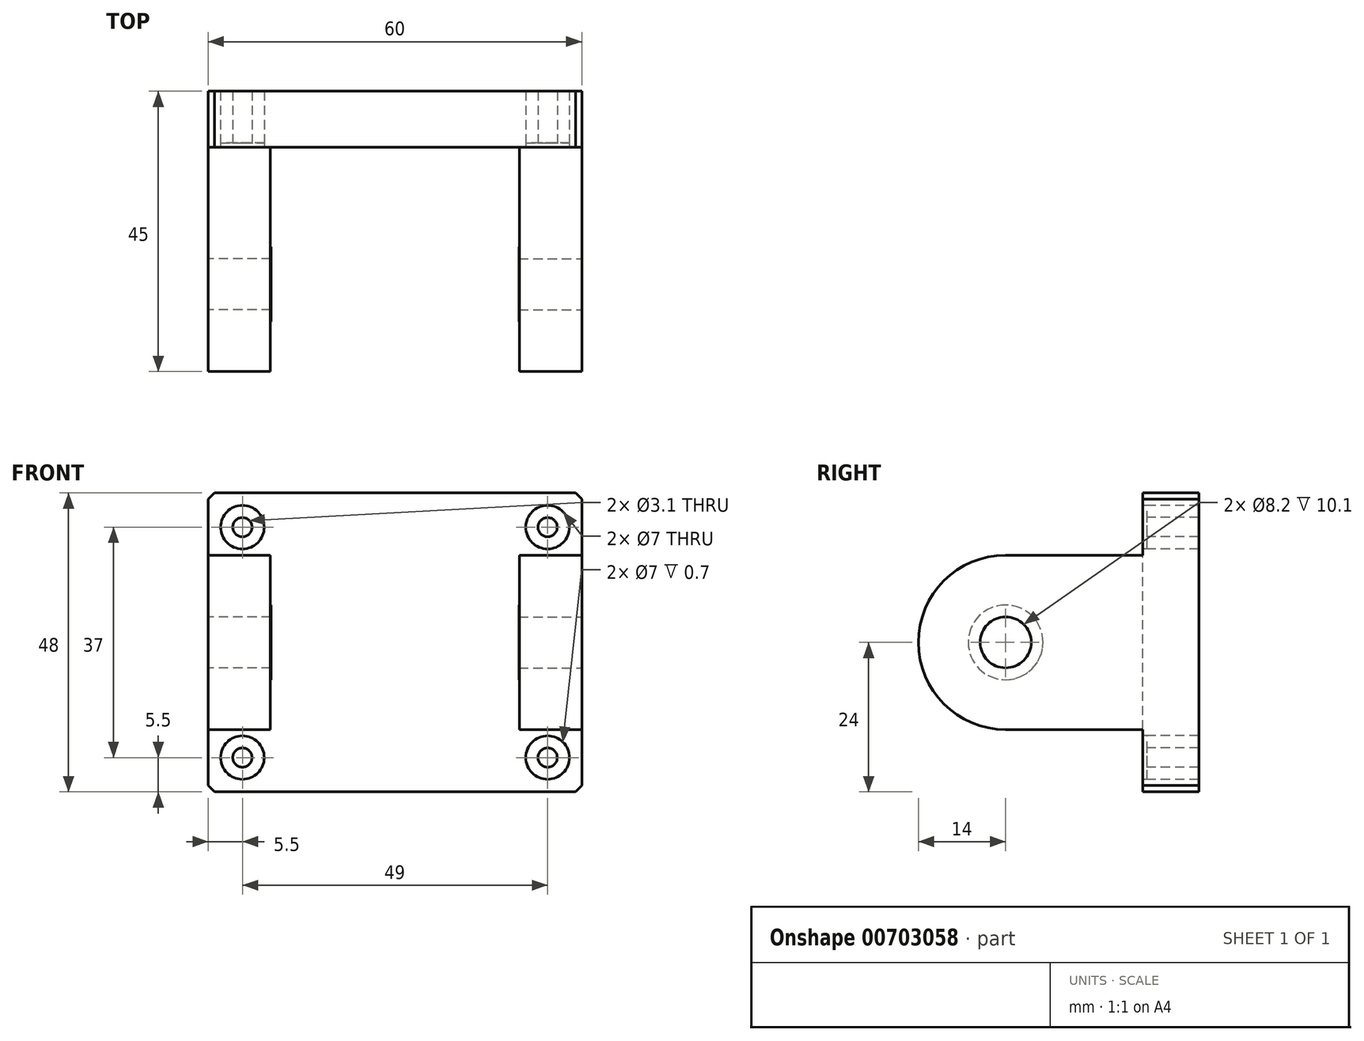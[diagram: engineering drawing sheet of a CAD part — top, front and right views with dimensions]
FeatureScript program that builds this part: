
annotation { "Feature Type Name" : "Feature", "Feature Type Description" : "" }
export const myFeature = defineFeature(function(context is Context, id is Id, definition is map)
    precondition{}
    {
        {
            var Q0;
            Q0=qCreatedBy(makeId("Front.planeOp"),FACE);
            var sketch = newSketch(context, id + "F0", { "sketchPlane" : qUnion([Q0])});
            skLineSegment(sketch, "E0.bottom", {"start": v(-20, 14) * mm, "end": v(20, 14) * mm});
            skLineSegment(sketch, "E0.top", {"start": v(-20, -14) * mm, "end": v(20, -14) * mm});
            skLineSegment(sketch, "E0.left", {"start": v(-20, 14) * mm, "end": v(-20, -14) * mm});
            skLineSegment(sketch, "E0.right", {"start": v(20, 14) * mm, "end": v(20, -14) * mm});
            skPoint(sketch, "E0.middle", {"position": v(0, 0) * mm});
            skLineSegment(sketch, "E1.0", {"start": v(-30, 24) * mm, "end": v(30, 24) * mm});
            skLineSegment(sketch, "E1.1", {"start": v(-30, 24) * mm, "end": v(-30, -24) * mm});
            skLineSegment(sketch, "E1.2", {"start": v(-30, -24) * mm, "end": v(30, -24) * mm});
            skLineSegment(sketch, "E1.3", {"start": v(30, 24) * mm, "end": v(30, -24) * mm});
            skSolve(sketch);
        }
        {
            var Q0;
            Q0=makeQuery(id+"F0.imprint","IMPRINT",FACE,{"disambiguationData":[TD([[makeQuery(id+"F0.imprint","IMPRINT",EDGE,{"derivedFrom":sQuery(id+"F0.wireOp",EDGE,"E0.bottom")}),1.0]])]});
            extrude(context, id + "F1", {"entities" : qUnion([Q0]), "depth" : 46 * mm, "offsetDistance" : 25 * mm});
        }
        {
            var Q0;
            Q0=makeQuery(id+"F1.opExtrude","SWEPT_FACE",FACE,{"disambiguationData":[OSD([sQuery(id+"F0.wireOp",EDGE,"E1.1")])]});
            var sketch = newSketch(context, id + "F2", { "sketchPlane" : qUnion([Q0])});
            skLineSegment(sketch, "E2", {"start": v(31, 24) * mm, "end": v(31, -24) * mm, "construction": true});
            skCircle(sketch, "E3", {"center": v(31, 0) * mm, "radius": 4.1 * mm});
            skSolve(sketch);
        }
        {
            var Q0;
            Q0=makeQuery(id+"F2.imprint","IMPRINT",FACE,{"disambiguationData":[TD([[makeQuery(id+"F2.imprint","IMPRINT",EDGE,{"derivedFrom":sQuery(id+"F2.wireOp",EDGE,"E3")}),1.0]])]});
            extrude(context, id + "F3", {"entities" : qUnion([Q0]), "operationType" : NewBodyOperationType.REMOVE, "oppositeDirection" : true, "depth" : 10 * mm, "offsetDistance" : 25 * mm});
        }
        {
            var Q0;
            Q0=makeQuery(id+"F1.opExtrude","SWEPT_FACE",FACE,{"disambiguationData":[OSD([sQuery(id+"F0.wireOp",EDGE,"E1.3")])]});
            var sketch = newSketch(context, id + "F4", { "sketchPlane" : qUnion([Q0])});
            skLineSegment(sketch, "E4", {"start": v(-31, -24) * mm, "end": v(-31, 24) * mm, "construction": true});
            skCircle(sketch, "E5", {"center": v(-31, 0) * mm, "radius": 4.1 * mm});
            skSolve(sketch);
        }
        {
            var Q0;
            Q0=makeQuery(id+"F4.imprint","IMPRINT",FACE,{"disambiguationData":[TD([[makeQuery(id+"F4.imprint","IMPRINT",EDGE,{"derivedFrom":sQuery(id+"F4.wireOp",EDGE,"E5")}),1.0]])]});
            extrude(context, id + "F5", {"entities" : qUnion([Q0]), "operationType" : NewBodyOperationType.REMOVE, "oppositeDirection" : true, "depth" : 10 * mm, "offsetDistance" : 25 * mm});
        }
        {
            var Q0;
            Q0=makeQuery(id+"F1.opExtrude","SWEPT_FACE",FACE,{"disambiguationData":[OSD([sQuery(id+"F0.wireOp",EDGE,"E0.left")])]});
            var sketch = newSketch(context, id + "F6", { "sketchPlane" : qUnion([Q0])});
            skCircle(sketch, "E6", {"center": v(-31, 0) * mm, "radius": 6 * mm});
            skSolve(sketch);
        }
        {
            var Q0;
            Q0=makeQuery(id+"F6.imprint","IMPRINT",FACE,{"disambiguationData":[TD([[makeQuery(id+"F6.imprint","IMPRINT",EDGE,{"derivedFrom":sQuery(id+"F6.wireOp",EDGE,"E6")}),1.0]])]});
            extrude(context, id + "F7", {"entities" : qUnion([Q0]), "operationType" : NewBodyOperationType.ADD, "depth" : 0.1 * mm, "offsetDistance" : 25 * mm});
        }
        {
            var Q0;
            Q0=makeQuery(id+"F1.opExtrude","SWEPT_FACE",FACE,{"disambiguationData":[OSD([sQuery(id+"F0.wireOp",EDGE,"E0.right")])]});
            var sketch = newSketch(context, id + "F8", { "sketchPlane" : qUnion([Q0])});
            skCircle(sketch, "E7", {"center": v(31, 0) * mm, "radius": 6 * mm});
            skSolve(sketch);
        }
        {
            var Q0;
            Q0=makeQuery(id+"F8.imprint","IMPRINT",FACE,{"disambiguationData":[TD([[makeQuery(id+"F8.imprint","IMPRINT",EDGE,{"derivedFrom":sQuery(id+"F8.wireOp",EDGE,"E7")}),1.0]])]});
            extrude(context, id + "F9", {"entities" : qUnion([Q0]), "operationType" : NewBodyOperationType.ADD, "depth" : 0.1 * mm, "offsetDistance" : 25 * mm});
        }
        {
            var Q0;
            Q0=makeQuery(id+"F1.opExtrude","CAP_FACE",FACE,{"disambiguationData":[OSD([sQuery(id+"F0.wireOp",EDGE,"E0.bottom"),sQuery(id+"F0.wireOp",EDGE,"E0.top"),sQuery(id+"F0.wireOp",EDGE,"E0.left"),sQuery(id+"F0.wireOp",EDGE,"E0.right"),sQuery(id+"F0.wireOp",EDGE,"E1.0"),sQuery(id+"F0.wireOp",EDGE,"E1.1"),sQuery(id+"F0.wireOp",EDGE,"E1.2"),sQuery(id+"F0.wireOp",EDGE,"E1.3")])],"isStart":false});
            var sketch = newSketch(context, id + "F10", { "sketchPlane" : qUnion([Q0])});
            skLineSegment(sketch, "E8", {"start": v(-20, 14) * mm, "end": v(-20, 24) * mm});
            skLineSegment(sketch, "E9", {"start": v(20, 14) * mm, "end": v(20, 24) * mm});
            skLineSegment(sketch, "E10", {"start": v(-20, -14) * mm, "end": v(-20, -24) * mm});
            skLineSegment(sketch, "E11", {"start": v(20, -14) * mm, "end": v(20, -24) * mm});
            skSolve(sketch);
        }
        {
            var Q0;
            {var subQ0=sQuery(id+"F10.wireOp",EDGE,"E8");Q0=makeQuery(id+"F10.imprint","IMPRINT",FACE,{"disambiguationData":[TD([[makeQuery(id+"F10.imprint","IMPRINT",EDGE,{"derivedFrom":subQ0}),-1.0]])]});}
            var Q1;
            {var subQ0=sQuery(id+"F10.wireOp",EDGE,"E10");Q1=makeQuery(id+"F10.imprint","IMPRINT",FACE,{"disambiguationData":[TD([[makeQuery(id+"F10.imprint","IMPRINT",EDGE,{"derivedFrom":subQ0}),1.0]])]});}
            extrude(context, id + "F11", {"entities" : qUnion([Q0, Q1]), "operationType" : NewBodyOperationType.REMOVE, "oppositeDirection" : true, "depth" : 15 * mm, "offsetDistance" : 25 * mm});
        }
        {
            var Q0;
            Q0=makeQuery(id+"F11.boolean.opBoolean","MERGE",FACE,{"derivedFrom":[makeQuery(id+"F1.opExtrude","SWEPT_FACE",FACE,{"disambiguationData":[OSD([sQuery(id+"F0.wireOp",EDGE,"E0.right")])]}),makeQuery(id+"F11.opExtrude","SWEPT_FACE",FACE,{"disambiguationData":[OSD([sQuery(id+"F10.wireOp",EDGE,"E9")])]}),makeQuery(id+"F11.opExtrude","SWEPT_FACE",FACE,{"disambiguationData":[OSD([sQuery(id+"F10.wireOp",EDGE,"E11")])]})]});
            var sketch = newSketch(context, id + "F12", { "sketchPlane" : qUnion([Q0])});
            skArc(sketch, "E12", {"start": v(31, -14) * mm, "mid": v(45, 0) * mm, "end": v(31, 14) * mm});
            skSolve(sketch);
        }
        {
            var Q0;
            Q0=makeQuery(id+"F11.boolean.opBoolean","MERGE",FACE,{"derivedFrom":[makeQuery(id+"F1.opExtrude","SWEPT_FACE",FACE,{"disambiguationData":[OSD([sQuery(id+"F0.wireOp",EDGE,"E0.left")])]}),makeQuery(id+"F11.opExtrude","SWEPT_FACE",FACE,{"disambiguationData":[OSD([sQuery(id+"F10.wireOp",EDGE,"E8")])]}),makeQuery(id+"F11.opExtrude","SWEPT_FACE",FACE,{"disambiguationData":[OSD([sQuery(id+"F10.wireOp",EDGE,"E10")])]})]});
            var sketch = newSketch(context, id + "F13", { "sketchPlane" : qUnion([Q0])});
            skArc(sketch, "E13", {"start": v(-31, 14) * mm, "mid": v(-45, 0) * mm, "end": v(-31, -14) * mm});
            skSolve(sketch);
        }
        {
            var Q0;
            Q0=makeQuery(id+"F13.imprint","IMPRINT",FACE,{"disambiguationData":[TD([[makeQuery(id+"F13.imprint","IMPRINT",EDGE,{"derivedFrom":sQuery(id+"F13.wireOp",EDGE,"E13")}),-1.0]])]});
            extrude(context, id + "F14", {"entities" : qUnion([Q0]), "operationType" : NewBodyOperationType.REMOVE, "oppositeDirection" : true, "depth" : 10 * mm, "offsetDistance" : 25 * mm});
        }
        {
            var Q0;
            Q0=makeQuery(id+"F12.imprint","IMPRINT",FACE,{"disambiguationData":[TD([[makeQuery(id+"F12.imprint","IMPRINT",EDGE,{"derivedFrom":sQuery(id+"F12.wireOp",EDGE,"E12")}),-1.0]])]});
            extrude(context, id + "F15", {"entities" : qUnion([Q0]), "operationType" : NewBodyOperationType.REMOVE, "oppositeDirection" : true, "depth" : 10 * mm, "offsetDistance" : 25 * mm});
        }
        {
            var Q0;
            {var subQ0=sQuery(id+"F10.wireOp",EDGE,"E11");var subQ1=sQuery(id+"F10.wireOp",EDGE,"E10");Q0=makeQuery(id+"F15.boolean.opBoolean","MERGE",FACE,{"derivedFrom":[makeQuery(id+"F14.boolean.opBoolean","MERGE",FACE,{"derivedFrom":[makeQuery(id+"F11.boolean.opBoolean","COPY",FACE,{"derivedFrom":makeQuery(id+"F11.opExtrude","CAP_FACE",FACE,{"disambiguationData":[OSD([sQuery(id+"F0.wireOp",EDGE,"E0.top"),sQuery(id+"F0.wireOp",EDGE,"E1.2"),subQ1,subQ0])],"isStart":false})}),makeQuery(id+"F14.opExtrude","SWEPT_FACE",FACE,{"disambiguationData":[OSD([subQ1])]})]}),makeQuery(id+"F15.opExtrude","SWEPT_FACE",FACE,{"disambiguationData":[OSD([subQ0])]})]});}
            extrude(context, id + "F16", {"entities" : qUnion([Q0]), "operationType" : NewBodyOperationType.REMOVE, "oppositeDirection" : true, "depth" : 22 * mm, "offsetDistance" : 25 * mm});
        }
        {
            var Q0;
            {var subQ0=sQuery(id+"F10.wireOp",EDGE,"E9");var subQ1=sQuery(id+"F10.wireOp",EDGE,"E8");Q0=makeQuery(id+"F15.boolean.opBoolean","MERGE",FACE,{"derivedFrom":[makeQuery(id+"F14.boolean.opBoolean","MERGE",FACE,{"derivedFrom":[makeQuery(id+"F11.boolean.opBoolean","COPY",FACE,{"derivedFrom":makeQuery(id+"F11.opExtrude","CAP_FACE",FACE,{"disambiguationData":[OSD([sQuery(id+"F0.wireOp",EDGE,"E0.bottom"),sQuery(id+"F0.wireOp",EDGE,"E1.0"),subQ1,subQ0])],"isStart":false})}),makeQuery(id+"F14.opExtrude","SWEPT_FACE",FACE,{"disambiguationData":[OSD([subQ1])]})]}),makeQuery(id+"F15.opExtrude","SWEPT_FACE",FACE,{"disambiguationData":[OSD([subQ0])]})]});}
            extrude(context, id + "F17", {"entities" : qUnion([Q0]), "operationType" : NewBodyOperationType.REMOVE, "oppositeDirection" : true, "depth" : 22 * mm, "offsetDistance" : 25 * mm});
        }
        {
            var Q0;
            Q0=makeQuery(id+"F17.boolean.opBoolean","COPY",EDGE,{"derivedFrom":makeQuery(id+"F17.opExtrude","CAP_EDGE",EDGE,{"disambiguationData":[OSD([sQuery(id+"F10.wireOp",EDGE,"E9")])],"isStart":false})});
            var Q1;
            Q1=makeQuery(id+"F1.opExtrude","SWEPT_EDGE",EDGE,{"disambiguationData":[OSD([sQuery(id+"F0.wireOp",EDGE,"E1.0"),sQuery(id+"F0.wireOp",EDGE,"E1.3")])]});
            var Q2;
            Q2=makeQuery(id+"F17.boolean.opBoolean","COPY",EDGE,{"derivedFrom":makeQuery(id+"F17.opExtrude","CAP_EDGE",EDGE,{"disambiguationData":[OSD([sQuery(id+"F0.wireOp",EDGE,"E1.0"),sQuery(id+"F10.wireOp",EDGE,"E8"),sQuery(id+"F10.wireOp",EDGE,"E9")])],"isStart":false})});
            var Q3;
            Q3=makeQuery(id+"F1.opExtrude","SWEPT_EDGE",EDGE,{"disambiguationData":[OSD([sQuery(id+"F0.wireOp",EDGE,"E1.0"),sQuery(id+"F0.wireOp",EDGE,"E1.1")])]});
            var Q4;
            Q4=makeQuery(id+"F17.boolean.opBoolean","COPY",EDGE,{"derivedFrom":makeQuery(id+"F17.opExtrude","CAP_EDGE",EDGE,{"disambiguationData":[OSD([sQuery(id+"F10.wireOp",EDGE,"E8")])],"isStart":false})});
            var Q5;
            Q5=makeQuery(id+"F16.boolean.opBoolean","COPY",EDGE,{"derivedFrom":makeQuery(id+"F16.opExtrude","CAP_EDGE",EDGE,{"disambiguationData":[OSD([sQuery(id+"F10.wireOp",EDGE,"E11")])],"isStart":false})});
            var Q6;
            Q6=makeQuery(id+"F1.opExtrude","SWEPT_EDGE",EDGE,{"disambiguationData":[OSD([sQuery(id+"F0.wireOp",EDGE,"E1.2"),sQuery(id+"F0.wireOp",EDGE,"E1.3")])]});
            var Q7;
            Q7=makeQuery(id+"F16.boolean.opBoolean","COPY",EDGE,{"derivedFrom":makeQuery(id+"F16.opExtrude","CAP_EDGE",EDGE,{"disambiguationData":[OSD([sQuery(id+"F0.wireOp",EDGE,"E1.2"),sQuery(id+"F10.wireOp",EDGE,"E10"),sQuery(id+"F10.wireOp",EDGE,"E11")])],"isStart":false})});
            var Q8;
            Q8=makeQuery(id+"F1.opExtrude","SWEPT_EDGE",EDGE,{"disambiguationData":[OSD([sQuery(id+"F0.wireOp",EDGE,"E1.1"),sQuery(id+"F0.wireOp",EDGE,"E1.2")])]});
            var Q9;
            Q9=makeQuery(id+"F16.boolean.opBoolean","COPY",EDGE,{"derivedFrom":makeQuery(id+"F16.opExtrude","CAP_EDGE",EDGE,{"disambiguationData":[OSD([sQuery(id+"F10.wireOp",EDGE,"E10")])],"isStart":false})});
            chamfer(context, id + "F18", {"entities" : qUnion([Q0, Q1, Q2, Q3, Q4, Q5, Q6, Q7, Q8, Q9]), "width" : 1 * mm, "tangentPropagation" : true});
        }
        {
            var Q0;
            Q0=makeQuery(id+"F17.boolean.opBoolean","COPY",FACE,{"derivedFrom":makeQuery(id+"F17.opExtrude","CAP_FACE",FACE,{"disambiguationData":[OSD([sQuery(id+"F0.wireOp",EDGE,"E0.bottom"),sQuery(id+"F0.wireOp",EDGE,"E1.0"),sQuery(id+"F10.wireOp",EDGE,"E8"),sQuery(id+"F10.wireOp",EDGE,"E9")])],"isStart":false})});
            var sketch = newSketch(context, id + "F19", { "sketchPlane" : qUnion([Q0])});
            skCircle(sketch, "E14", {"center": v(-24.5, 18.5) * mm, "radius": 1.55 * mm});
            skPoint(sketch, "E14.centerSnap0", {"position": v(-24.5, 14) * mm});
            skPoint(sketch, "E14.centerSnap1", {"position": v(-29, 18.5) * mm});
            skCircle(sketch, "E15.MirrorC", {"center": v(24.5, 18.5) * mm, "radius": 1.55 * mm});
            skCircle(sketch, "E16.MirrorC", {"center": v(-24.5, -18.5) * mm, "radius": 1.55 * mm});
            skCircle(sketch, "E17.MirrorC", {"center": v(24.5, -18.5) * mm, "radius": 1.55 * mm});
            skCircle(sketch, "E18", {"center": v(-24.5, 18.5) * mm, "radius": 3.5 * mm});
            skCircle(sketch, "E19.MirrorC", {"center": v(24.5, 18.5) * mm, "radius": 3.5 * mm});
            skCircle(sketch, "E20.MirrorC", {"center": v(-24.5, -18.5) * mm, "radius": 3.5 * mm});
            skCircle(sketch, "E21.MirrorC", {"center": v(24.5, -18.5) * mm, "radius": 3.5 * mm});
            skSolve(sketch);
        }
        {
            var Q0;
            Q0=makeQuery(id+"F19.imprint","IMPRINT",FACE,{"disambiguationData":[TD([[makeQuery(id+"F19.imprint","IMPRINT",EDGE,{"derivedFrom":sQuery(id+"F19.wireOp",EDGE,"E14")}),1.0]])]});
            var Q1;
            Q1=makeQuery(id+"F19.imprint","IMPRINT",FACE,{"disambiguationData":[TD([[makeQuery(id+"F19.imprint","IMPRINT",EDGE,{"derivedFrom":sQuery(id+"F19.wireOp",EDGE,"E15.MirrorC")}),-1.0]])]});
            var Q2;
            Q2=makeQuery(id+"F19.imprint","IMPRINT",FACE,{"disambiguationData":[TD([[makeQuery(id+"F19.imprint","IMPRINT",EDGE,{"derivedFrom":sQuery(id+"F19.wireOp",EDGE,"E16.MirrorC")}),-1.0]])]});
            var Q3;
            Q3=makeQuery(id+"F19.imprint","IMPRINT",FACE,{"disambiguationData":[TD([[makeQuery(id+"F19.imprint","IMPRINT",EDGE,{"derivedFrom":sQuery(id+"F19.wireOp",EDGE,"E17.MirrorC")}),1.0]])]});
            extrude(context, id + "F20", {"entities" : qUnion([Q0, Q1, Q2, Q3]), "operationType" : NewBodyOperationType.REMOVE, "oppositeDirection" : true, "depth" : 10 * mm, "offsetDistance" : 25 * mm});
        }
        {
            var Q0;
            Q0 = qSketchRegion(id + "F19", true);
            extrude(context, id + "F21", {"entities" : qUnion([Q0]), "operationType" : NewBodyOperationType.REMOVE, "oppositeDirection" : true, "depth" : 0.7 * mm, "offsetDistance" : 25 * mm});
        }
        {
            var Q0;
            Q0=makeQuery(id+"F1.opExtrude","SWEPT_FACE",FACE,{"disambiguationData":[OSD([sQuery(id+"F0.wireOp",EDGE,"E0.bottom")])]});
            var Q1;
            Q1=makeQuery(id+"F1.opExtrude","SWEPT_BODY",BODY,{"disambiguationData":[OSD([sQuery(id+"F0.wireOp",EDGE,"E0.bottom"),sQuery(id+"F0.wireOp",EDGE,"E0.top"),sQuery(id+"F0.wireOp",EDGE,"E0.left"),sQuery(id+"F0.wireOp",EDGE,"E0.right"),sQuery(id+"F0.wireOp",EDGE,"E1.0"),sQuery(id+"F0.wireOp",EDGE,"E1.1"),sQuery(id+"F0.wireOp",EDGE,"E1.2"),sQuery(id+"F0.wireOp",EDGE,"E1.3")])]});
            extrude(context, id + "F22", {"entities" : qUnion([Q0]), "operationType" : NewBodyOperationType.ADD, "endBound" : BoundingType.UP_TO_NEXT, "depth" : 10 * mm, "endBoundEntityBody" : qUnion([Q1]), "offsetDistance" : 25 * mm});
        }
    });
